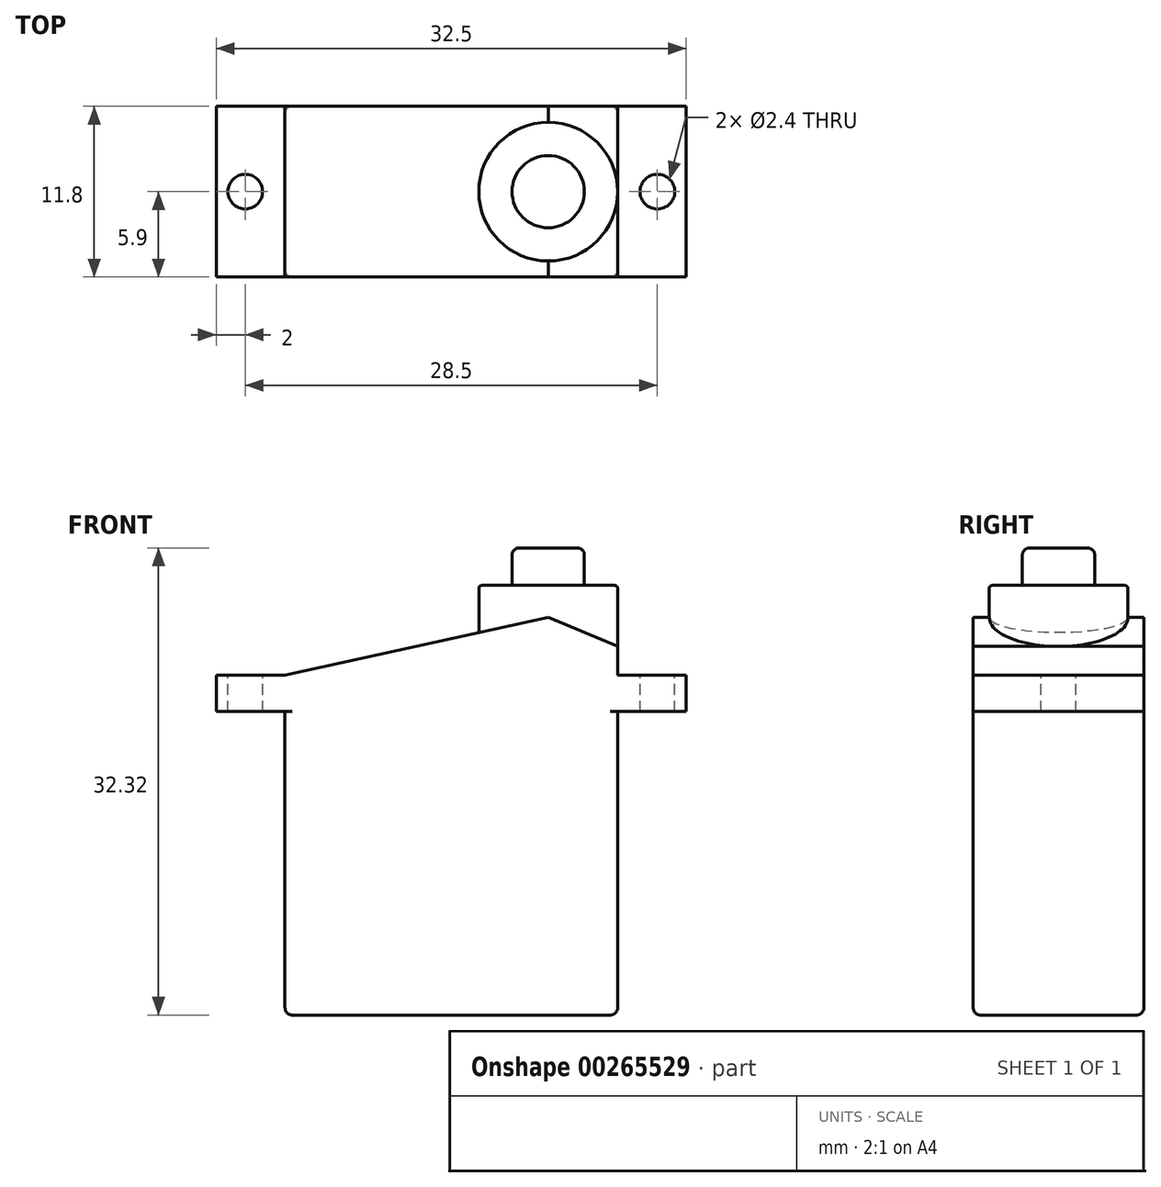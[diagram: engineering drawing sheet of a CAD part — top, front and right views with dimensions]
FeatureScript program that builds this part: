
annotation { "Feature Type Name" : "Feature", "Feature Type Description" : "" }
export const myFeature = defineFeature(function(context is Context, id is Id, definition is map)
    precondition{}
    {
        {
            var Q0;
            Q0=qCreatedBy(makeId("Front.planeOp"),FACE);
            var sketch = newSketch(context, id + "F0", { "sketchPlane" : qUnion([Q0])});
            skLineSegment(sketch, "E0", {"start": v(0, 0) * mm, "end": v(-23, 0) * mm});
            skLineSegment(sketch, "E1", {"start": v(-23, 0) * mm, "end": v(-23, 21) * mm});
            skLineSegment(sketch, "E2", {"start": v(-23, 21) * mm, "end": v(-27.75, 21) * mm});
            skLineSegment(sketch, "E3", {"start": v(-27.75, 21) * mm, "end": v(-27.75, 23.5) * mm});
            skLineSegment(sketch, "E4", {"start": v(0, 0) * mm, "end": v(0, 21) * mm});
            skLineSegment(sketch, "E5", {"start": v(0, 21) * mm, "end": v(4.75, 21) * mm});
            skLineSegment(sketch, "E6", {"start": v(4.75, 21) * mm, "end": v(4.75, 23.5) * mm});
            skLineSegment(sketch, "E7", {"start": v(4.75, 23.5) * mm, "end": v(0, 23.5) * mm});
            skLineSegment(sketch, "E8", {"start": v(0, 0) * mm, "end": v(-4.8, 0) * mm, "construction": true});
            skLineSegment(sketch, "E9", {"start": v(-4.8, 0) * mm, "end": v(-4.8, 27.5) * mm, "construction": true});
            skLineSegment(sketch, "E10", {"start": v(0, 23.5) * mm, "end": v(0, 25.5) * mm});
            skLineSegment(sketch, "E11", {"start": v(0, 25.5) * mm, "end": v(-4.8, 27.5) * mm});
            skLineSegment(sketch, "E12", {"start": v(-27.75, 23.5) * mm, "end": v(-23, 23.5) * mm});
            skLineSegment(sketch, "E13", {"start": v(-23, 23.5) * mm, "end": v(-4.8, 27.5) * mm});
            skSolve(sketch);
        }
        {
            var Q0;
            Q0=makeQuery(id+"F0.imprint","IMPRINT",FACE,{"disambiguationData":[TD([[makeQuery(id+"F0.imprint","IMPRINT",EDGE,{"derivedFrom":sQuery(id+"F0.wireOp",EDGE,"E0")}),-1.0]])]});
            extrude(context, id + "F1", {"entities" : qUnion([Q0]), "depth" : 11.8 * mm});
        }
        {
            var Q0;
            Q0=makeQuery(id+"F1.opExtrude","SWEPT_FACE",FACE,{"disambiguationData":[OSD([sQuery(id+"F0.wireOp",EDGE,"E12")])]});
            var sketch = newSketch(context, id + "F2", { "sketchPlane" : qUnion([Q0])});
            skLineSegment(sketch, "E14", {"start": v(-27.75, 0) * mm, "end": v(-27.75, -5.9) * mm, "construction": true});
            skLineSegment(sketch, "E15", {"start": v(0, 0) * mm, "end": v(0, -5.9) * mm, "construction": true});
            skCircle(sketch, "E16", {"center": v(-25.75, -5.9) * mm, "radius": 1.2 * mm});
            skCircle(sketch, "E17", {"center": v(2.75, -5.9) * mm, "radius": 1.2 * mm});
            skLineSegment(sketch, "E18", {"start": v(-27.75, -5.9) * mm, "end": v(-25.75, -5.9) * mm, "construction": true});
            skLineSegment(sketch, "E19", {"start": v(0, -5.9) * mm, "end": v(2.75, -5.9) * mm, "construction": true});
            skSolve(sketch);
        }
        {
            var Q0;
            Q0=makeQuery(id+"F2.imprint","IMPRINT",FACE,{"disambiguationData":[TD([[makeQuery(id+"F2.imprint","IMPRINT",EDGE,{"derivedFrom":sQuery(id+"F2.wireOp",EDGE,"E17")}),1.0]])]});
            var Q1;
            Q1=makeQuery(id+"F2.imprint","IMPRINT",FACE,{"disambiguationData":[TD([[makeQuery(id+"F2.imprint","IMPRINT",EDGE,{"derivedFrom":sQuery(id+"F2.wireOp",EDGE,"E16")}),1.0]])]});
            extrude(context, id + "F3", {"entities" : qUnion([Q0, Q1]), "operationType" : NewBodyOperationType.REMOVE, "oppositeDirection" : true, "depth" : 4 * mm});
        }
        {
            var Q0;
            Q0=sQuery(id+"F0.wireOp",VERTEX,"E11.end");
            var Q1;
            Q1=makeQuery(id+"F1.opExtrude","SWEPT_FACE",FACE,{"disambiguationData":[OSD([sQuery(id+"F0.wireOp",EDGE,"E0")])]});
            cPlane(context, id + "F4", {"entities" : qUnion([Q0, Q1]), "cplaneType" : CPlaneType.PLANE_POINT, "offset" : 25 * mm, "width" : 150 * mm, "height" : 150 * mm});
        }
        {
            var Q0;
            Q0=qCreatedBy(id+"F4.planeOp",FACE);
            var sketch = newSketch(context, id + "F5", { "sketchPlane" : qUnion([Q0])});
            skLineSegment(sketch, "E20", {"start": v(-4.8, 0) * mm, "end": v(-4.8, 5.9) * mm, "construction": true});
            skCircle(sketch, "E21", {"center": v(-4.8, 5.9) * mm, "radius": 4.8 * mm});
            skSolve(sketch);
        }
        {
            var Q0;
            Q0=makeQuery(id+"F5.imprint","IMPRINT",FACE,{"disambiguationData":[TD([[makeQuery(id+"F5.imprint","IMPRINT",EDGE,{"derivedFrom":sQuery(id+"F5.wireOp",EDGE,"E21")}),1.0]])]});
            var Q1;
            Q1=sQuery(id+"F5.wireOp",EDGE,"E21");
            extrude(context, id + "F6", {"entities" : qUnion([Q0]), "operationType" : NewBodyOperationType.ADD, "surfaceEntities" : qUnion([Q1]), "depth" : 25 * mm});
        }
        {
            var Q0;
            Q0=makeQuery(id+"F6.opExtrude","CAP_FACE",FACE,{"disambiguationData":[OSD([sQuery(id+"F5.wireOp",EDGE,"E21")])],"isStart":true});
            extrude(context, id + "F7", {"entities" : qUnion([Q0]), "operationType" : NewBodyOperationType.ADD, "depth" : 2.22 * mm});
        }
        {
            var Q0;
            Q0=makeQuery(id+"F7.opExtrude","CAP_FACE",FACE,{"disambiguationData":[OSD([sQuery(id+"F5.wireOp",EDGE,"E21")])],"isStart":false});
            var sketch = newSketch(context, id + "F8", { "sketchPlane" : qUnion([Q0])});
            skCircle(sketch, "E22", {"center": v(-4.8, -5.9) * mm, "radius": 2.5 * mm});
            skSolve(sketch);
        }
        {
            var Q0;
            Q0=makeQuery(id+"F8.imprint","IMPRINT",FACE,{"disambiguationData":[TD([[makeQuery(id+"F8.imprint","IMPRINT",EDGE,{"derivedFrom":sQuery(id+"F8.wireOp",EDGE,"E22")}),1.0]])]});
            extrude(context, id + "F9", {"entities" : qUnion([Q0]), "operationType" : NewBodyOperationType.ADD, "depth" : 2.6 * mm});
        }
        {
            var Q0;
            Q0=makeQuery(id+"F9.opExtrude","CAP_EDGE",EDGE,{"disambiguationData":[OSD([sQuery(id+"F8.wireOp",EDGE,"E22")])],"isStart":false});
            fillet(context, id + "F10", {"entities" : qUnion([Q0]), "radius" : 0.5 * mm, "tangentPropagation" : true, "allowEdgeOverflow" : false});
        }
        {
            var Q0;
            Q0=makeQuery(id+"F1.opExtrude","CAP_EDGE",EDGE,{"disambiguationData":[OSD([sQuery(id+"F0.wireOp",EDGE,"E1")])],"isStart":false});
            var Q1;
            Q1=makeQuery(id+"F1.opExtrude","CAP_EDGE",EDGE,{"disambiguationData":[OSD([sQuery(id+"F0.wireOp",EDGE,"E4")])],"isStart":false});
            var Q2;
            Q2=makeQuery(id+"F1.opExtrude","CAP_EDGE",EDGE,{"disambiguationData":[OSD([sQuery(id+"F0.wireOp",EDGE,"E4")])],"isStart":true});
            var Q3;
            Q3=makeQuery(id+"F1.opExtrude","CAP_EDGE",EDGE,{"disambiguationData":[OSD([sQuery(id+"F0.wireOp",EDGE,"E1")])],"isStart":true});
            var Q4;
            Q4=makeQuery(id+"F1.opExtrude","CAP_EDGE",EDGE,{"disambiguationData":[OSD([sQuery(id+"F0.wireOp",EDGE,"E0")])],"isStart":true});
            var Q5;
            Q5=makeQuery(id+"F1.opExtrude","SWEPT_EDGE",EDGE,{"disambiguationData":[OSD([sQuery(id+"F0.wireOp",EDGE,"E0"),sQuery(id+"F0.wireOp",EDGE,"E1")])]});
            var Q6;
            Q6=makeQuery(id+"F1.opExtrude","SWEPT_EDGE",EDGE,{"disambiguationData":[OSD([sQuery(id+"F0.wireOp",EDGE,"E0"),sQuery(id+"F0.wireOp",EDGE,"E4")])]});
            var Q7;
            Q7=makeQuery(id+"F1.opExtrude","CAP_EDGE",EDGE,{"disambiguationData":[OSD([sQuery(id+"F0.wireOp",EDGE,"E0")])],"isStart":false});
            fillet(context, id + "F11", {"entities" : qUnion([Q0, Q1, Q2, Q3, Q4, Q5, Q6, Q7]), "radius" : 0.5 * mm, "tangentPropagation" : true, "allowEdgeOverflow" : false});
        }
        {
            var Q0;
            Q0=makeQuery(id+"F7.opExtrude","CAP_EDGE",EDGE,{"disambiguationData":[OSD([sQuery(id+"F5.wireOp",EDGE,"E21")])],"isStart":false});
            fillet(context, id + "F12", {"entities" : qUnion([Q0]), "radius" : 0.2 * mm, "tangentPropagation" : true, "allowEdgeOverflow" : false});
        }
    });
